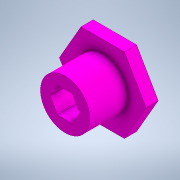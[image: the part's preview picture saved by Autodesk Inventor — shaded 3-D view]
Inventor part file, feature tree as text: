
AUTODESK INVENTOR PART (.ipt)
format: ipt  version: 2021.2 (Build 252289000, 289)  size: 140,800 bytes
history: native  units: in
note: dims shown in document units (in); Inventor stores cm internally (conversion verified against a paired STEP export)
features: extrude x2, other x2, sketch x1
ambient origin geometry x8: Origin, YZ Plane, XZ Plane, XY Plane, X Axis, Y Axis, Z Axis, Center Point
bodies: Solid1 (feature_tree)
feature tree (5):
  extrude  "Extrusion1"  Depth=1.0in
  extrude  "Extrusion3"  Depth=1.5in
  other  "Thicken Internal Hex Hold"
  other  "Reduce Size of Bushing Fitting"
  sketch  "Sketch1"  dims[d0=0.5in d2=1.0in d3=0.2113in d4=0.75in d5=0.0in d7=0.5in d10=1.5in d11=0.25in d12=0.0in d13=0.0075in d14=0.0075in d15=0.0075in d16=0.0075in]
